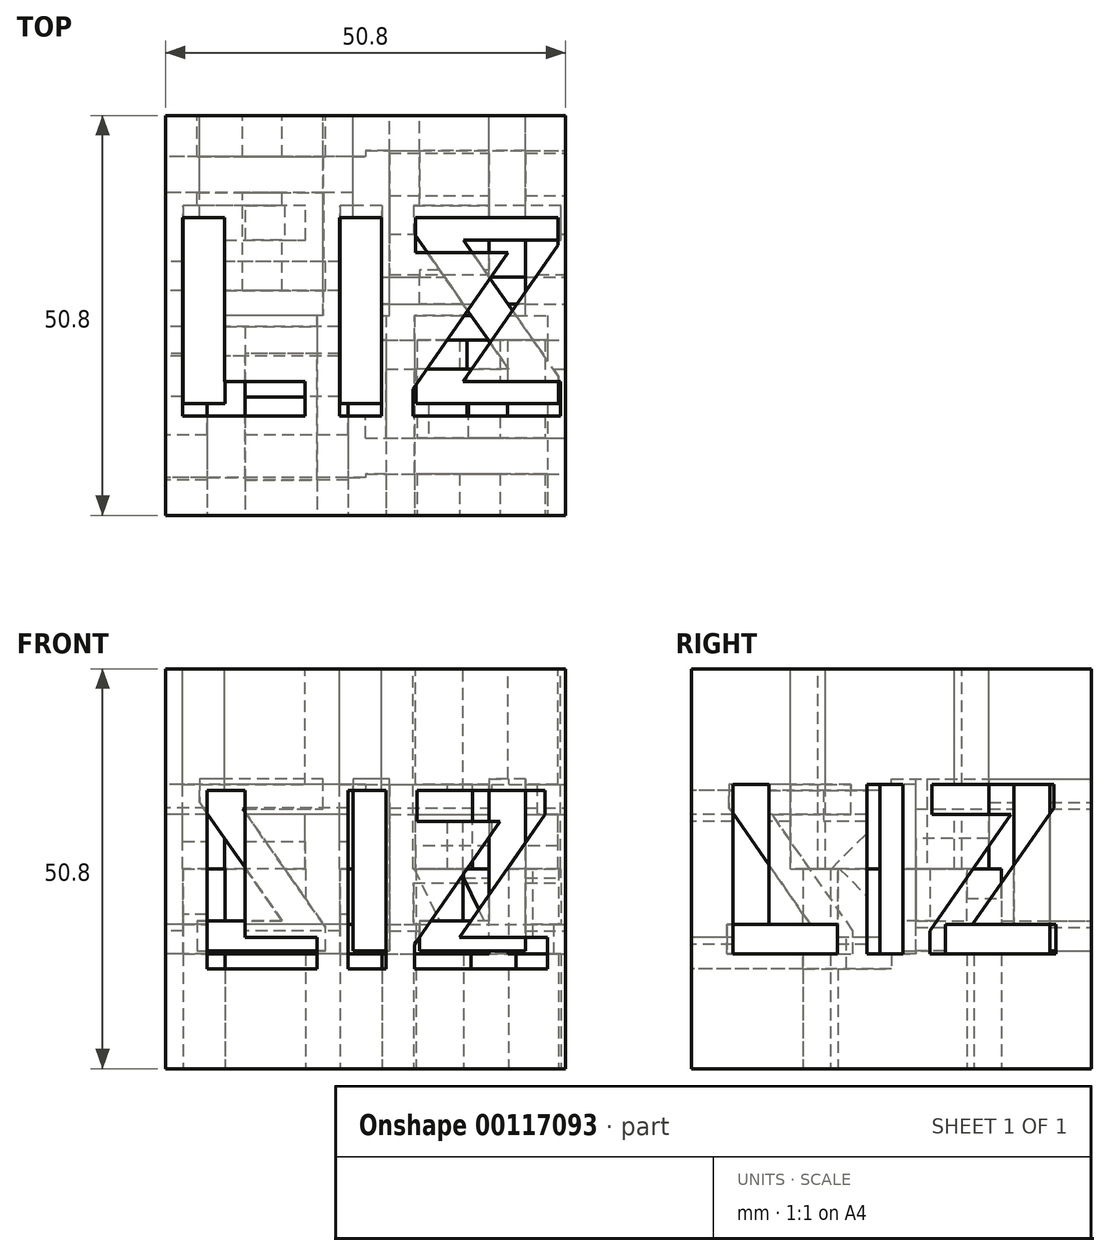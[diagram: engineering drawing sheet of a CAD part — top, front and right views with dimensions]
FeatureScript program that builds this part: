
annotation { "Feature Type Name" : "Feature", "Feature Type Description" : "" }
export const myFeature = defineFeature(function(context is Context, id is Id, definition is map)
    precondition{}
    {
        {
            var Q0;
            Q0=qCreatedBy(makeId("Front.planeOp"),FACE);
            var sketch = newSketch(context, id + "F0", { "sketchPlane" : qUnion([Q0])});
            skLineSegment(sketch, "E0.bottom", {"start": v(-25.4, 25.4) * mm, "end": v(25.4, 25.4) * mm});
            skLineSegment(sketch, "E0.top", {"start": v(-25.4, -25.4) * mm, "end": v(25.4, -25.4) * mm});
            skLineSegment(sketch, "E0.left", {"start": v(-25.4, 25.4) * mm, "end": v(-25.4, -25.4) * mm});
            skLineSegment(sketch, "E0.right", {"start": v(25.4, 25.4) * mm, "end": v(25.4, -25.4) * mm});
            skSolve(sketch);
        }
        {
            var Q0;
            Q0 = qSketchRegion(id + "F0", true);
            extrude(context, id + "F1", {"entities" : qUnion([Q0]), "depth" : 50.8 * mm});
        }
        {
            var Q0;
            Q0=makeQuery(id+"F1.opExtrude","SWEPT_FACE",FACE,{"disambiguationData":[OSD([sQuery(id+"F0.wireOp",EDGE,"E0.right")])]});
            var sketch = newSketch(context, id + "F2", { "sketchPlane" : qUnion([Q0])});
            skText(sketch, "E1", { "text": "LIZ\n", "fontName": "OpenSans-Bold.ttf"});
            const initialGuessF2  = {"E1": [-0.04826, -0.01084, 1, 0, 0.02171]};
            skSetInitialGuess(sketch, initialGuessF2);
            skSolve(sketch);
        }
        {
            var Q0;
            Q0 = qSketchRegion(id + "F2", true);
            extrude(context, id + "F3", {"entities" : qUnion([Q0]), "operationType" : NewBodyOperationType.REMOVE, "oppositeDirection" : true, "depth" : 25.4 * mm});
        }
        {
            var Q0;
            Q0=makeQuery(id+"F1.opExtrude","CAP_FACE",FACE,{"disambiguationData":[OSD([sQuery(id+"F0.wireOp",EDGE,"E0.bottom"),sQuery(id+"F0.wireOp",EDGE,"E0.top"),sQuery(id+"F0.wireOp",EDGE,"E0.left"),sQuery(id+"F0.wireOp",EDGE,"E0.right")])],"isStart":false});
            var sketch = newSketch(context, id + "F4", { "sketchPlane" : qUnion([Q0])});
            skText(sketch, "E2", { "text": "LIZ", "fontName": "OpenSans-Bold.ttf"});
            const initialGuessF4  = {"E2": [-0.02299, -0.0127, 1, 0, 0.02286]};
            skSetInitialGuess(sketch, initialGuessF4);
            skSolve(sketch);
        }
        {
            var Q0;
            Q0 = qSketchRegion(id + "F4", true);
            extrude(context, id + "F5", {"entities" : qUnion([Q0]), "operationType" : NewBodyOperationType.REMOVE, "oppositeDirection" : true, "depth" : 25.4 * mm});
        }
        {
            var Q0;
            Q0=makeQuery(id+"F1.opExtrude","CAP_FACE",FACE,{"disambiguationData":[OSD([sQuery(id+"F0.wireOp",EDGE,"E0.bottom"),sQuery(id+"F0.wireOp",EDGE,"E0.top"),sQuery(id+"F0.wireOp",EDGE,"E0.left"),sQuery(id+"F0.wireOp",EDGE,"E0.right")])],"isStart":true});
            var sketch = newSketch(context, id + "F6", { "sketchPlane" : qUnion([Q0])});
            skText(sketch, "E3", { "text": "LIZ", "fontName": "OpenSans-Bold.ttf"});
            const initialGuessF6  = {"E3": [-0.0231, -0.01045, 1, 0, 0.02207]};
            skSetInitialGuess(sketch, initialGuessF6);
            skSolve(sketch);
        }
        {
            var Q0;
            Q0 = qSketchRegion(id + "F6", true);
            extrude(context, id + "F7", {"entities" : qUnion([Q0]), "operationType" : NewBodyOperationType.REMOVE, "oppositeDirection" : true, "depth" : 25.4 * mm});
        }
        {
            var Q0;
            Q0=makeQuery(id+"F1.opExtrude","SWEPT_FACE",FACE,{"disambiguationData":[OSD([sQuery(id+"F0.wireOp",EDGE,"E0.left")])]});
            var sketch = newSketch(context, id + "F8", { "sketchPlane" : qUnion([Q0])});
            skText(sketch, "E4", { "text": "LIZ", "fontName": "OpenSans-Bold.ttf"});
            const initialGuessF8  = {"E4": [0.00254, -0.01084, 1, 0, 0.02171]};
            skSetInitialGuess(sketch, initialGuessF8);
            skSolve(sketch);
        }
        {
            var Q0;
            Q0 = qSketchRegion(id + "F8", true);
            extrude(context, id + "F9", {"entities" : qUnion([Q0]), "operationType" : NewBodyOperationType.REMOVE, "oppositeDirection" : true, "depth" : 25.4 * mm});
        }
        {
            var Q0;
            Q0=makeQuery(id+"F1.opExtrude","SWEPT_FACE",FACE,{"disambiguationData":[OSD([sQuery(id+"F0.wireOp",EDGE,"E0.bottom")])]});
            var sketch = newSketch(context, id + "F10", { "sketchPlane" : qUnion([Q0])});
            skText(sketch, "E5", { "text": "LIZ", "fontName": "OpenSans-Bold.ttf"});
            const initialGuessF10  = {"E5": [-0.02642, -0.0382, 1, 0, 0.0254]};
            skSetInitialGuess(sketch, initialGuessF10);
            skSolve(sketch);
        }
        {
            var Q0;
            Q0 = qSketchRegion(id + "F10", true);
            extrude(context, id + "F11", {"entities" : qUnion([Q0]), "operationType" : NewBodyOperationType.REMOVE, "oppositeDirection" : true, "depth" : 25.4 * mm});
        }
        {
            var Q0;
            Q0=makeQuery(id+"F1.opExtrude","SWEPT_FACE",FACE,{"disambiguationData":[OSD([sQuery(id+"F0.wireOp",EDGE,"E0.top")])]});
            var sketch = newSketch(context, id + "F12", { "sketchPlane" : qUnion([Q0])});
            skText(sketch, "E6", { "text": "LIZ", "fontName": "OpenSans-Bold.ttf"});
            const initialGuessF12  = {"E6": [-0.02637, 0.01143, 1, 0, 0.0254]};
            skSetInitialGuess(sketch, initialGuessF12);
            skSolve(sketch);
        }
        {
            var Q0;
            Q0 = qSketchRegion(id + "F12", true);
            extrude(context, id + "F13", {"entities" : qUnion([Q0]), "operationType" : NewBodyOperationType.REMOVE, "oppositeDirection" : true, "depth" : 25.4 * mm});
        }
    });
